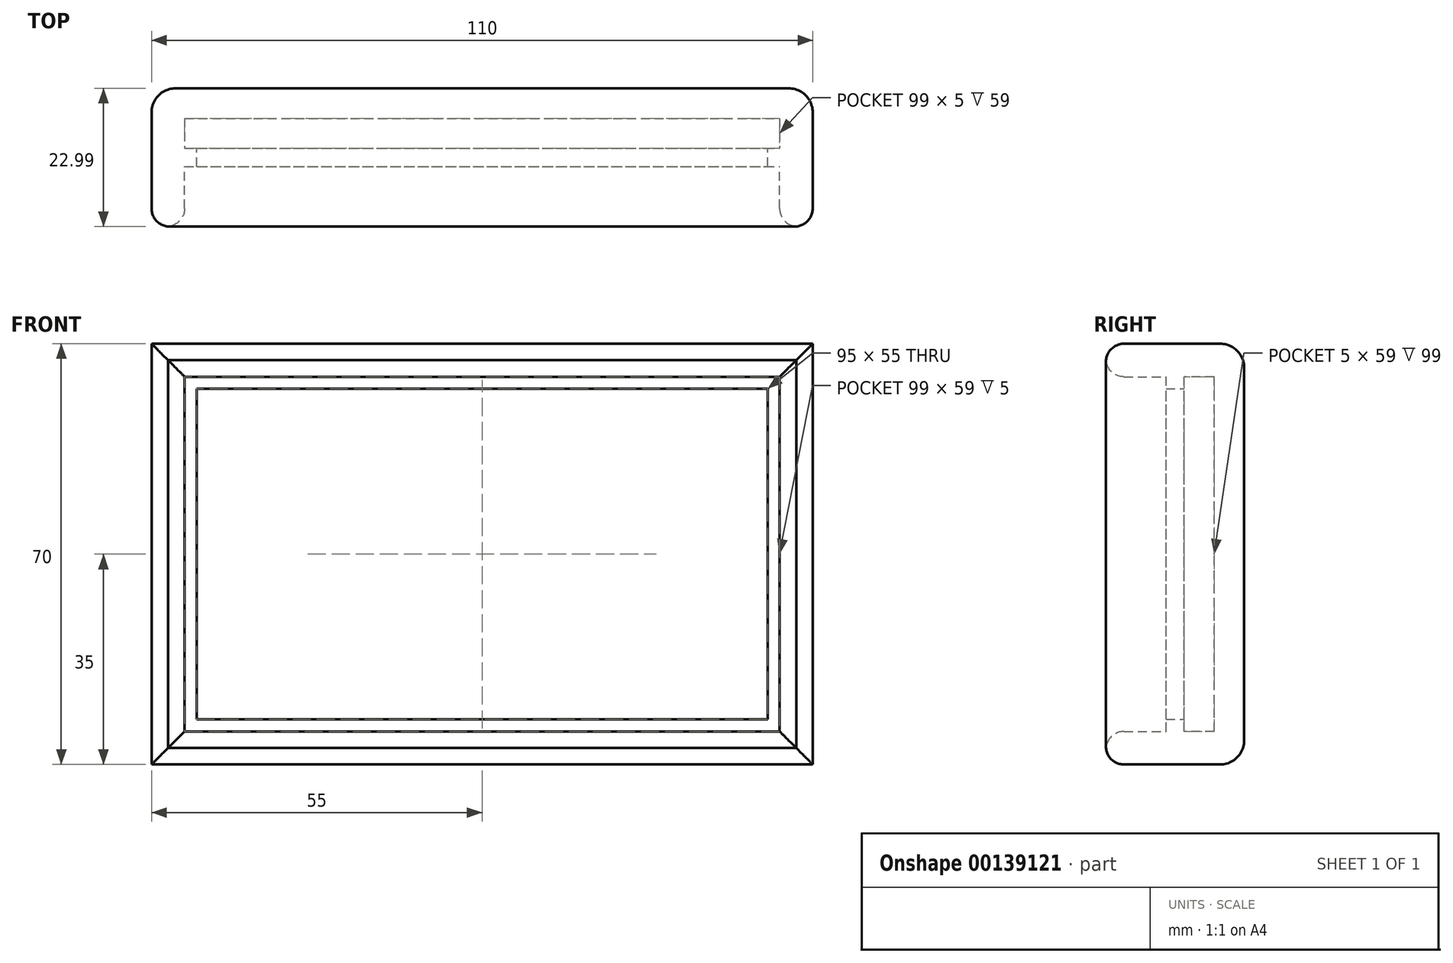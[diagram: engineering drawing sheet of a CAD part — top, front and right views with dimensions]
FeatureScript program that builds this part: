
annotation { "Feature Type Name" : "Feature", "Feature Type Description" : "" }
export const myFeature = defineFeature(function(context is Context, id is Id, definition is map)
    precondition{}
    {
        {
            var Q0;
            Q0=qCreatedBy(makeId("Front.planeOp"),FACE);
            var sketch = newSketch(context, id + "F0", { "sketchPlane" : qUnion([Q0])});
            skLineSegment(sketch, "E0.bottom", {"start": v(-55, -35) * mm, "end": v(55, -35) * mm});
            skLineSegment(sketch, "E0.top", {"start": v(-55, 35) * mm, "end": v(55, 35) * mm});
            skLineSegment(sketch, "E0.left", {"start": v(-55, -35) * mm, "end": v(-55, 35) * mm});
            skLineSegment(sketch, "E0.right", {"start": v(55, -35) * mm, "end": v(55, 35) * mm});
            skPoint(sketch, "E0.middle", {"position": v(0, 0) * mm});
            skLineSegment(sketch, "E1", {"start": v(0, 35) * mm, "end": v(0, -35) * mm});
            skSolve(sketch);
        }
        {
            var Q0;
            {var subQ0=sQuery(id+"F0.wireOp",EDGE,"E0.left");Q0=makeQuery(id+"F0.imprint","IMPRINT",FACE,{"disambiguationData":[TD([[makeQuery(id+"F0.imprint","IMPRINT",EDGE,{"derivedFrom":subQ0}),-1.0]])]});}
            var Q1;
            {var subQ0=sQuery(id+"F0.wireOp",EDGE,"E0.right");Q1=makeQuery(id+"F0.imprint","IMPRINT",FACE,{"disambiguationData":[TD([[makeQuery(id+"F0.imprint","IMPRINT",EDGE,{"derivedFrom":subQ0}),1.0]])]});}
            extrude(context, id + "F1", {"entities" : qUnion([Q0, Q1]), "depth" : 10 * mm});
        }
        {
            var Q0;
            Q0=makeQuery(id+"F1.opExtrude","CAP_FACE",FACE,{"disambiguationData":[OSD([sQuery(id+"F0.wireOp",EDGE,"E0.bottom"),sQuery(id+"F0.wireOp",EDGE,"E0.top"),sQuery(id+"F0.wireOp",EDGE,"E0.left"),sQuery(id+"F0.wireOp",EDGE,"E0.right")])],"isStart":false});
            var sketch = newSketch(context, id + "F2", { "sketchPlane" : qUnion([Q0])});
            skPoint(sketch, "E2.middle", {"position": v(1.5, 0) * mm});
            skLineSegment(sketch, "E3.bottom", {"start": v(-49.5, -29.5) * mm, "end": v(49.5, -29.5) * mm});
            skLineSegment(sketch, "E3.top", {"start": v(-49.5, 29.5) * mm, "end": v(49.5, 29.5) * mm});
            skLineSegment(sketch, "E3.left", {"start": v(-49.5, -29.5) * mm, "end": v(-49.5, 29.5) * mm});
            skLineSegment(sketch, "E3.right", {"start": v(49.5, -29.5) * mm, "end": v(49.5, 29.5) * mm});
            skPoint(sketch, "E3.middle", {"position": v(0, 0) * mm});
            skSolve(sketch);
        }
        {
            var Q0;
            Q0=makeQuery(id+"F2.imprint","IMPRINT",FACE,{"disambiguationData":[TD([[makeQuery(id+"F2.imprint","IMPRINT",EDGE,{"derivedFrom":sQuery(id+"F2.wireOp",EDGE,"E3.bottom")}),1.0]])]});
            extrude(context, id + "F3", {"entities" : qUnion([Q0]), "operationType" : NewBodyOperationType.REMOVE, "oppositeDirection" : true, "depth" : 5 * mm});
        }
        {
            var Q0;
            Q0=makeQuery(id+"F1.opExtrude","CAP_FACE",FACE,{"disambiguationData":[OSD([sQuery(id+"F0.wireOp",EDGE,"E0.bottom"),sQuery(id+"F0.wireOp",EDGE,"E0.top"),sQuery(id+"F0.wireOp",EDGE,"E0.left"),sQuery(id+"F0.wireOp",EDGE,"E0.right")])],"isStart":false});
            var sketch = newSketch(context, id + "F4", { "sketchPlane" : qUnion([Q0])});
            skLineSegment(sketch, "E4.bottom", {"start": v(-55, -35) * mm, "end": v(55, -35) * mm});
            skLineSegment(sketch, "E4.top", {"start": v(-55, 35) * mm, "end": v(55, 35) * mm});
            skLineSegment(sketch, "E4.left", {"start": v(-55, -35) * mm, "end": v(-55, 35) * mm});
            skLineSegment(sketch, "E4.right", {"start": v(55, -35) * mm, "end": v(55, 35) * mm});
            skPoint(sketch, "E4.middle", {"position": v(0, 0) * mm});
            skLineSegment(sketch, "E5.bottom", {"start": v(-47.5, -27.5) * mm, "end": v(47.5, -27.5) * mm});
            skLineSegment(sketch, "E5.top", {"start": v(-47.5, 27.5) * mm, "end": v(47.5, 27.5) * mm});
            skLineSegment(sketch, "E5.left", {"start": v(-47.5, -27.5) * mm, "end": v(-47.5, 27.5) * mm});
            skLineSegment(sketch, "E5.right", {"start": v(47.5, -27.5) * mm, "end": v(47.5, 27.5) * mm});
            skSolve(sketch);
        }
        {
            var Q0;
            Q0=makeQuery(id+"F4.imprint","IMPRINT",FACE,{"disambiguationData":[TD([[makeQuery(id+"F4.imprint","IMPRINT",EDGE,{"derivedFrom":sQuery(id+"F4.wireOp",EDGE,"E5.bottom")}),-1.0]])]});
            var Q1;
            Q1=makeQuery(id+"F4.imprint","IMPRINT",FACE,{"disambiguationData":[TD([[makeQuery(id+"F4.imprint","IMPRINT",EDGE,{"derivedFrom":sQuery(id+"F4.wireOp",EDGE,"E4.bottom")}),1.0]])]});
            extrude(context, id + "F5", {"entities" : qUnion([Q0, Q1]), "operationType" : NewBodyOperationType.ADD, "depth" : 3 * mm});
        }
        {
            var Q0;
            Q0=makeQuery(id+"F5.opExtrude","CAP_FACE",FACE,{"disambiguationData":[OSD([sQuery(id+"F4.wireOp",EDGE,"E4.bottom"),sQuery(id+"F4.wireOp",EDGE,"E4.top"),sQuery(id+"F4.wireOp",EDGE,"E4.left"),sQuery(id+"F4.wireOp",EDGE,"E4.right"),sQuery(id+"F4.wireOp",EDGE,"E5.bottom"),sQuery(id+"F4.wireOp",EDGE,"E5.top"),sQuery(id+"F4.wireOp",EDGE,"E5.left"),sQuery(id+"F4.wireOp",EDGE,"E5.right")])],"isStart":false});
            var sketch = newSketch(context, id + "F6", { "sketchPlane" : qUnion([Q0])});
            skLineSegment(sketch, "E6.bottom", {"start": v(-55, -35) * mm, "end": v(55, -35) * mm});
            skLineSegment(sketch, "E6.top", {"start": v(-55, 35) * mm, "end": v(55, 35) * mm});
            skLineSegment(sketch, "E6.left", {"start": v(-55, -35) * mm, "end": v(-55, 35) * mm});
            skLineSegment(sketch, "E6.right", {"start": v(55, -35) * mm, "end": v(55, 35) * mm});
            skPoint(sketch, "E6.middle", {"position": v(0, 0) * mm});
            skLineSegment(sketch, "E7.bottom", {"start": v(-49.5, -29.5) * mm, "end": v(49.5, -29.5) * mm});
            skLineSegment(sketch, "E7.top", {"start": v(-49.5, 29.5) * mm, "end": v(49.5, 29.5) * mm});
            skLineSegment(sketch, "E7.left", {"start": v(-49.5, -29.5) * mm, "end": v(-49.5, 29.5) * mm});
            skLineSegment(sketch, "E7.right", {"start": v(49.5, -29.5) * mm, "end": v(49.5, 29.5) * mm});
            skSolve(sketch);
        }
        {
            var Q0;
            Q0=makeQuery(id+"F6.imprint","IMPRINT",FACE,{"disambiguationData":[TD([[makeQuery(id+"F6.imprint","IMPRINT",EDGE,{"derivedFrom":sQuery(id+"F6.wireOp",EDGE,"E6.bottom")}),1.0]])]});
            extrude(context, id + "F7", {"entities" : qUnion([Q0]), "operationType" : NewBodyOperationType.ADD, "depth" : 10 * mm});
        }
        {
            var Q0;
            Q0=makeQuery(id+"F1.opExtrude","CAP_EDGE",EDGE,{"disambiguationData":[OSD([sQuery(id+"F0.wireOp",EDGE,"E0.top")])],"isStart":true});
            var Q1;
            Q1=makeQuery(id+"F1.opExtrude","CAP_EDGE",EDGE,{"disambiguationData":[OSD([sQuery(id+"F0.wireOp",EDGE,"E0.left")])],"isStart":true});
            var Q2;
            Q2=makeQuery(id+"F1.opExtrude","CAP_EDGE",EDGE,{"disambiguationData":[OSD([sQuery(id+"F0.wireOp",EDGE,"E0.right")])],"isStart":true});
            var Q3;
            Q3=makeQuery(id+"F1.opExtrude","CAP_EDGE",EDGE,{"disambiguationData":[OSD([sQuery(id+"F0.wireOp",EDGE,"E0.bottom")])],"isStart":true});
            fillet(context, id + "F8", {"entities" : qUnion([Q0, Q1, Q2, Q3]), "radius" : 4 * mm, "tangentPropagation" : true, "allowEdgeOverflow" : false});
        }
        {
            var Q0;
            Q0=makeQuery(id+"F7.opExtrude","CAP_EDGE",EDGE,{"disambiguationData":[OSD([sQuery(id+"F6.wireOp",EDGE,"E6.left")])],"isStart":false});
            var Q1;
            Q1=makeQuery(id+"F7.opExtrude","CAP_EDGE",EDGE,{"disambiguationData":[OSD([sQuery(id+"F6.wireOp",EDGE,"E6.top")])],"isStart":false});
            var Q2;
            Q2=makeQuery(id+"F7.opExtrude","CAP_EDGE",EDGE,{"disambiguationData":[OSD([sQuery(id+"F6.wireOp",EDGE,"E6.bottom")])],"isStart":false});
            var Q3;
            Q3=makeQuery(id+"F7.opExtrude","CAP_EDGE",EDGE,{"disambiguationData":[OSD([sQuery(id+"F6.wireOp",EDGE,"E6.right")])],"isStart":false});
            fillet(context, id + "F9", {"entities" : qUnion([Q0, Q1, Q2, Q3]), "radius" : 3 * mm, "tangentPropagation" : true, "allowEdgeOverflow" : false});
        }
        {
            var Q0;
            Q0=makeQuery(id+"F7.opExtrude","CAP_EDGE",EDGE,{"disambiguationData":[OSD([sQuery(id+"F6.wireOp",EDGE,"E7.left")])],"isStart":false});
            var Q1;
            Q1=makeQuery(id+"F7.opExtrude","CAP_EDGE",EDGE,{"disambiguationData":[OSD([sQuery(id+"F6.wireOp",EDGE,"E7.top")])],"isStart":false});
            var Q2;
            Q2=makeQuery(id+"F7.opExtrude","CAP_EDGE",EDGE,{"disambiguationData":[OSD([sQuery(id+"F6.wireOp",EDGE,"E7.bottom")])],"isStart":false});
            var Q3;
            Q3=makeQuery(id+"F7.opExtrude","CAP_EDGE",EDGE,{"disambiguationData":[OSD([sQuery(id+"F6.wireOp",EDGE,"E7.right")])],"isStart":false});
            fillet(context, id + "F10", {"entities" : qUnion([Q0, Q1, Q2, Q3]), "radius" : 3 * mm, "tangentPropagation" : true, "allowEdgeOverflow" : false});
        }
    });
